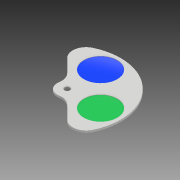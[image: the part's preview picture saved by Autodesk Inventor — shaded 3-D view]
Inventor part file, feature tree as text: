
AUTODESK INVENTOR PART (.ipt)
format: ipt  version: 2017 (Build 210142000, 142)  size: 151,552 bytes
history: native  units: mm
features: sketch x2, extrude x1, fillet x1, revolve x1, pattern_circular x1, projected_geometry x1
ambient origin geometry x8: Origin, YZ Plane, XZ Plane, XY Plane, X Axis, Y Axis, Z Axis, Center Point
bodies: Solid1 (feature_tree)
feature tree (7):
  extrude  "Extrusion1"  Depth=50.0mm
  fillet  "Fillet1"  Radius=30.0mm
  revolve  "Revolution1"  [1 undecoded]
  pattern_circular  "Circular Pattern1"  [2 undecoded]
  sketch  "Sketch1"  dims[d0=50.0mm d1=50.0mm d2=30.0mm]
  sketch  "Sketch2"  dims[d3=45.0deg d4=100.0mm d5=8.0mm d6=30.0mm d7=3.0mm d8=0.0mm d9=20.0mm d10=2.0mm d11=90.0deg d12=20.0mm d13=90.0deg]
  projected_geometry  "Projected Loop1"
note: 3 required parameter values undecoded (feature->parameter linkage not recoverable at this tier; creation-order binding heuristic only, values carry confidence <= 0.55)